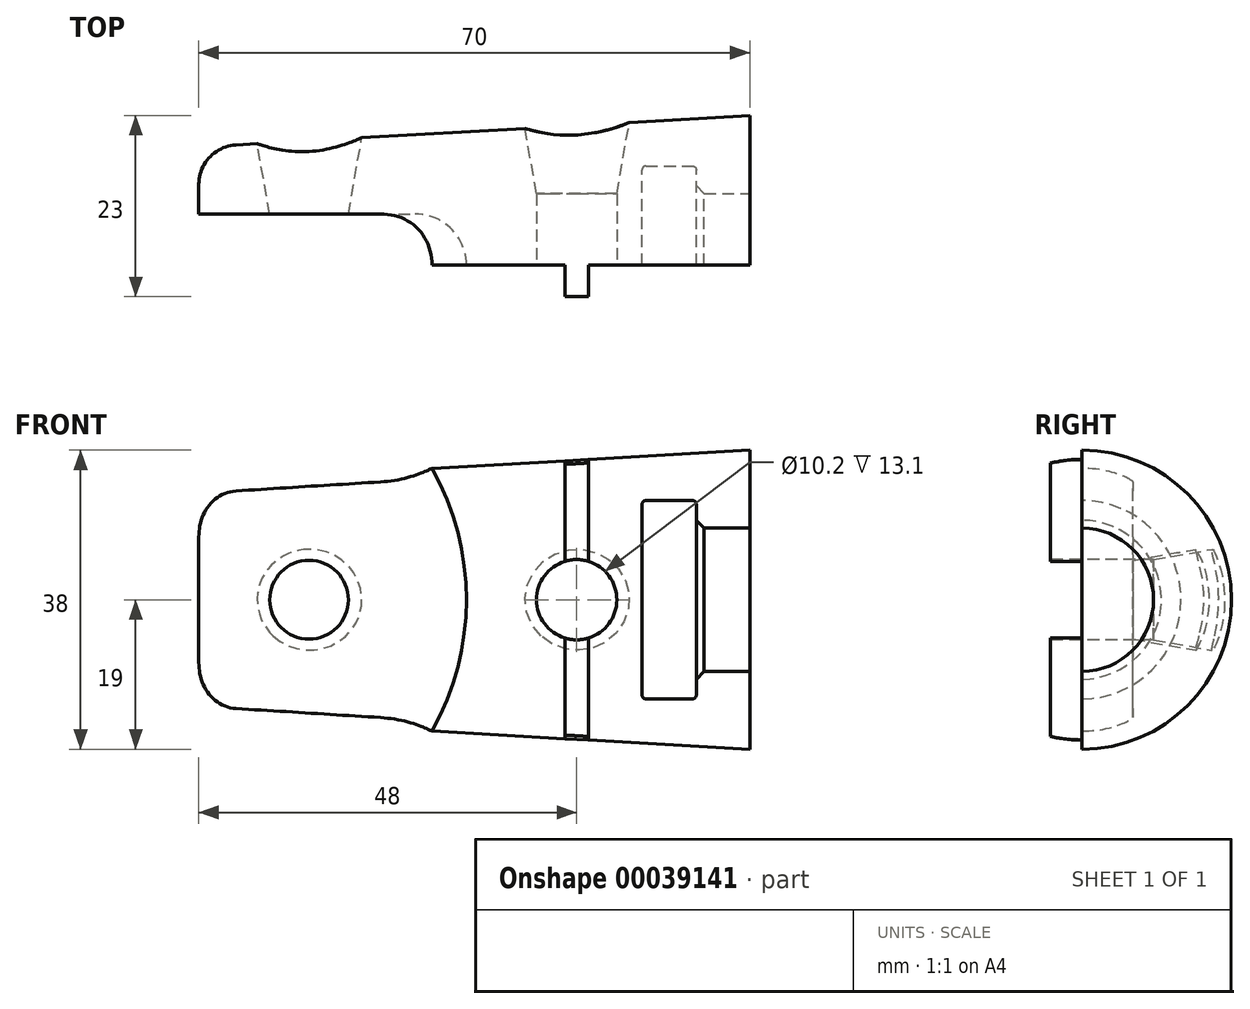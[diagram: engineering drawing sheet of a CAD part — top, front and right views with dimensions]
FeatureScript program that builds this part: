
annotation { "Feature Type Name" : "Feature", "Feature Type Description" : "" }
export const myFeature = defineFeature(function(context is Context, id is Id, definition is map)
    precondition{}
    {
        {
            var Q0;
            Q0=qCreatedBy(makeId("Front.planeOp"),FACE);
            var sketch = newSketch(context, id + "F0", { "sketchPlane" : qUnion([Q0])});
            skLineSegment(sketch, "E0", {"start": v(0, 19) * mm, "end": v(-70, 15) * mm});
            skLineSegment(sketch, "E1", {"start": v(-70, 15) * mm, "end": v(-70, 0) * mm});
            skLineSegment(sketch, "E2", {"start": v(-70, 0) * mm, "end": v(0, 0) * mm});
            skLineSegment(sketch, "E3", {"start": v(0, 0) * mm, "end": v(0, 19) * mm});
            skLineSegment(sketch, "E4.MirrorCS", {"start": v(0, 0) * mm, "end": v(0, -19) * mm, "construction": true});
            skLineSegment(sketch, "E5.MirrorCS", {"start": v(0, -19) * mm, "end": v(-70, -15) * mm, "construction": true});
            skLineSegment(sketch, "E6.MirrorCS", {"start": v(-70, -15) * mm, "end": v(-70, 0) * mm, "construction": true});
            skSolve(sketch);
        }
        {
            var Q0;
            Q0=makeQuery(id+"F0.imprint","IMPRINT",FACE,{"disambiguationData":[TD([[makeQuery(id+"F0.imprint","IMPRINT",EDGE,{"derivedFrom":sQuery(id+"F0.wireOp",EDGE,"E0")}),1.0]])]});
            var Q1;
            Q1=sQuery(id+"F0.wireOp",EDGE,"E2");
            revolve(context, id + "F1", {"entities" : qUnion([Q0]), "axis" : qUnion([Q1]), "revolveType" : RevolveType.FULL});
        }
        {
            var Q0;
            Q0=makeQuery(id+"F1.opRevolve","SWEPT_EDGE",EDGE,{"disambiguationData":[OSD([sQuery(id+"F0.wireOp",EDGE,"E0"),sQuery(id+"F0.wireOp",EDGE,"E1")])]});
            fillet(context, id + "F2", {"entities" : qUnion([Q0]), "radius" : 5 * mm, "tangentPropagation" : true, "allowEdgeOverflow" : false});
        }
        {
            var Q0;
            Q0=qCreatedBy(makeId("Top.planeOp"),FACE);
            var sketch = newSketch(context, id + "F3", { "sketchPlane" : qUnion([Q0])});
            skLineSegment(sketch, "E7", {"start": v(-70, 20.86) * mm, "end": v(-70, 0) * mm, "construction": true});
            skLineSegment(sketch, "E8", {"start": v(-70, 6.5) * mm, "end": v(-42.5, 6.5) * mm});
            skArc(sketch, "E9", {"start": v(-42.5, 6.5) * mm, "mid": v(-36, 0) * mm, "end": v(-42.5, -6.5) * mm});
            skLineSegment(sketch, "E10", {"start": v(-42.5, -6.5) * mm, "end": v(-70, -6.5) * mm});
            skLineSegment(sketch, "E11", {"start": v(0, 0) * mm, "end": v(-70, 0) * mm, "construction": true});
            skLineSegment(sketch, "E12", {"start": v(-70, 6.5) * mm, "end": v(-70, -6.5) * mm});
            skSolve(sketch);
        }
        {
            var Q0;
            Q0 = qSketchRegion(id + "F3", true);
            var Q1;
            Q1=sQuery(id+"F3.wireOp",EDGE,"E7");
            revolve(context, id + "F4", {"operationType" : NewBodyOperationType.REMOVE, "entities" : qUnion([Q0]), "axis" : qUnion([Q1]), "revolveType" : RevolveType.FULL, "oppositeDirection" : true});
        }
        {
            var Q0;
            Q0=qCreatedBy(makeId("Top.planeOp"),FACE);
            var sketch = newSketch(context, id + "F5", { "sketchPlane" : qUnion([Q0])});
            skLineSegment(sketch, "E13", {"start": v(-70, 0) * mm, "end": v(-23.5, 0) * mm});
            skLineSegment(sketch, "E14", {"start": v(-23.5, 0) * mm, "end": v(-23.5, -4) * mm});
            skLineSegment(sketch, "E15", {"start": v(-23.5, -4) * mm, "end": v(-20.5, -4) * mm});
            skLineSegment(sketch, "E16", {"start": v(-20.5, -4) * mm, "end": v(-20.5, 0) * mm});
            skLineSegment(sketch, "E17", {"start": v(-20.5, 0) * mm, "end": v(0, 0) * mm});
            skLineSegment(sketch, "E18", {"start": v(0, 0) * mm, "end": v(0, -19) * mm});
            skLineSegment(sketch, "E19", {"start": v(0, -19) * mm, "end": v(-70, -19) * mm});
            skLineSegment(sketch, "E20", {"start": v(-70, 0) * mm, "end": v(-70, -19) * mm});
            skLineSegment(sketch, "E21", {"start": v(-22, -4) * mm, "end": v(-22, 0) * mm, "construction": true});
            skLineSegment(sketch, "E22.MirrorCS", {"start": v(0, 19) * mm, "end": v(-70, 19) * mm, "construction": true});
            skSolve(sketch);
        }
        {
            var Q0;
            Q0 = qSketchRegion(id + "F5", true);
            extrude(context, id + "F6", {"entities" : qUnion([Q0]), "operationType" : NewBodyOperationType.REMOVE, "endBound" : BoundingType.THROUGH_ALL, "oppositeDirection" : true, "depth" : 25 * mm, "hasSecondDirection" : true, "secondDirectionBound" : BoundingType.THROUGH_ALL, "secondDirectionOppositeDirection" : false, "secondDirectionDepth" : 25 * mm});
        }
        {
            var Q0;
            Q0=qCreatedBy(makeId("Top.planeOp"),FACE);
            var sketch = newSketch(context, id + "F7", { "sketchPlane" : qUnion([Q0])});
            skLineSegment(sketch, "E23", {"start": v(0, 0) * mm, "end": v(0, 9.1) * mm});
            skLineSegment(sketch, "E24", {"start": v(0, 9.1) * mm, "end": v(-6.8, 9.1) * mm});
            skLineSegment(sketch, "E25", {"start": v(-7.3, 12.6) * mm, "end": v(-13.2, 12.6) * mm});
            skLineSegment(sketch, "E26", {"start": v(-13.7, 12.1) * mm, "end": v(-13.7, 0) * mm});
            skLineSegment(sketch, "E27", {"start": v(-13.7, 0) * mm, "end": v(0, 0) * mm});
            skLineSegment(sketch, "E28.MirrorCS", {"start": v(0, -9.1) * mm, "end": v(-6.8, -9.1) * mm, "construction": true});
            skLineSegment(sketch, "E29.MirrorCS", {"start": v(-6.8, -9.1) * mm, "end": v(-6.8, -12.6) * mm, "construction": true});
            skLineSegment(sketch, "E30.MirrorCS", {"start": v(-6.8, -12.6) * mm, "end": v(-13.7, -12.6) * mm, "construction": true});
            skPoint(sketch, "E31.visualSharp", {"position": v(-6.8, 12.6) * mm});
            skArc(sketch, "E31.filletArc", {"start": v(-6.8, 12.1) * mm, "mid": v(-6.95, 12.45) * mm, "end": v(-7.3, 12.6) * mm});
            skPoint(sketch, "E32.visualSharp", {"position": v(-13.7, 12.6) * mm});
            skArc(sketch, "E32.filletArc", {"start": v(-13.2, 12.6) * mm, "mid": v(-13.55, 12.45) * mm, "end": v(-13.7, 12.1) * mm});
            skLineSegment(sketch, "E33", {"start": v(-6.8, 12.1) * mm, "end": v(-6.8, 9.1) * mm});
            skSolve(sketch);
        }
        {
            var Q0;
            Q0 = qSketchRegion(id + "F7", true);
            var Q1;
            Q1=sQuery(id+"F7.wireOp",EDGE,"E27");
            revolve(context, id + "F8", {"operationType" : NewBodyOperationType.REMOVE, "entities" : qUnion([Q0]), "axis" : qUnion([Q1]), "revolveType" : RevolveType.FULL, "oppositeDirection" : true});
        }
        {
            var Q0;
            Q0=qCreatedBy(makeId("Top.planeOp"),FACE);
            var sketch = newSketch(context, id + "F9", { "sketchPlane" : qUnion([Q0])});
            skLineSegment(sketch, "E34", {"start": v(-28.88, 19.22) * mm, "end": v(-27.1, 9.1) * mm});
            skLineSegment(sketch, "E35", {"start": v(-27.1, 9.1) * mm, "end": v(-27.1, -4) * mm});
            skLineSegment(sketch, "E36", {"start": v(-27.1, -4) * mm, "end": v(-22, -4) * mm});
            skLineSegment(sketch, "E37", {"start": v(-22, -4) * mm, "end": v(-22, 19.22) * mm, "construction": true});
            skLineSegment(sketch, "E38", {"start": v(-22, 19.22) * mm, "end": v(-28.88, 19.22) * mm});
            skLineSegment(sketch, "E39", {"start": v(-22, 19.22) * mm, "end": v(-22, -4) * mm});
            skLineSegment(sketch, "E40.MirrorCS", {"start": v(-15.12, 19.22) * mm, "end": v(-16.9, 9.1) * mm, "construction": true});
            skLineSegment(sketch, "E41.MirrorCS", {"start": v(-16.9, 9.1) * mm, "end": v(-16.9, -4) * mm, "construction": true});
            skSolve(sketch);
        }
        {
            var Q0;
            Q0=makeQuery(id+"F9.imprint","IMPRINT",FACE,{"disambiguationData":[TD([[makeQuery(id+"F9.imprint","IMPRINT",EDGE,{"derivedFrom":sQuery(id+"F9.wireOp",EDGE,"E34")}),1.0]])]});
            var Q1;
            Q1=sQuery(id+"F9.wireOp",EDGE,"E39");
            revolve(context, id + "F10", {"operationType" : NewBodyOperationType.REMOVE, "entities" : qUnion([Q0]), "axis" : qUnion([Q1]), "revolveType" : RevolveType.FULL, "oppositeDirection" : true});
        }
        {
            var Q0;
            Q0=qCreatedBy(makeId("Top.planeOp"),FACE);
            var sketch = newSketch(context, id + "F11", { "sketchPlane" : qUnion([Q0])});
            skLineSegment(sketch, "E42", {"start": v(-56, 21.98) * mm, "end": v(-63.73, 21.98) * mm});
            skLineSegment(sketch, "E43", {"start": v(-63.73, 21.98) * mm, "end": v(-61, 6.5) * mm});
            skLineSegment(sketch, "E44", {"start": v(-56, 6.5) * mm, "end": v(-56, 21.98) * mm});
            skLineSegment(sketch, "E45", {"start": v(-61, 6.5) * mm, "end": v(-56, 6.5) * mm});
            skLineSegment(sketch, "E46.MirrorCS", {"start": v(-48.27, 21.98) * mm, "end": v(-51, 6.5) * mm, "construction": true});
            skSolve(sketch);
        }
        {
            var Q0;
            Q0=makeQuery(id+"F11.imprint","IMPRINT",FACE,{"disambiguationData":[TD([[makeQuery(id+"F11.imprint","IMPRINT",EDGE,{"derivedFrom":sQuery(id+"F11.wireOp",EDGE,"E42")}),1.0]])]});
            var Q1;
            Q1=sQuery(id+"F11.wireOp",EDGE,"E44");
            revolve(context, id + "F12", {"operationType" : NewBodyOperationType.REMOVE, "entities" : qUnion([Q0]), "axis" : qUnion([Q1]), "revolveType" : RevolveType.FULL, "oppositeDirection" : true});
        }
        {
            var Q0;
            Q0=makeQuery(id+"F8.boolean.opBoolean","COPY",EDGE,{"derivedFrom":makeQuery(id+"F8.opRevolve","SWEPT_EDGE",EDGE,{"disambiguationData":[OSD([sQuery(id+"F7.wireOp",EDGE,"E24"),sQuery(id+"F7.wireOp",EDGE,"E33")])]})});
            var Q1;
            Q1=makeQuery(id+"F8.boolean.opBoolean","COPY",EDGE,{"derivedFrom":makeQuery(id+"F8.opRevolve","SWEPT_EDGE",EDGE,{"disambiguationData":[OSD([sQuery(id+"F7.wireOp",EDGE,"E23"),sQuery(id+"F7.wireOp",EDGE,"E24")])]})});
            chamfer(context, id + "F13", {"entities" : qUnion([Q0, Q1]), "width" : 1 * mm, "tangentPropagation" : true});
        }
    });
